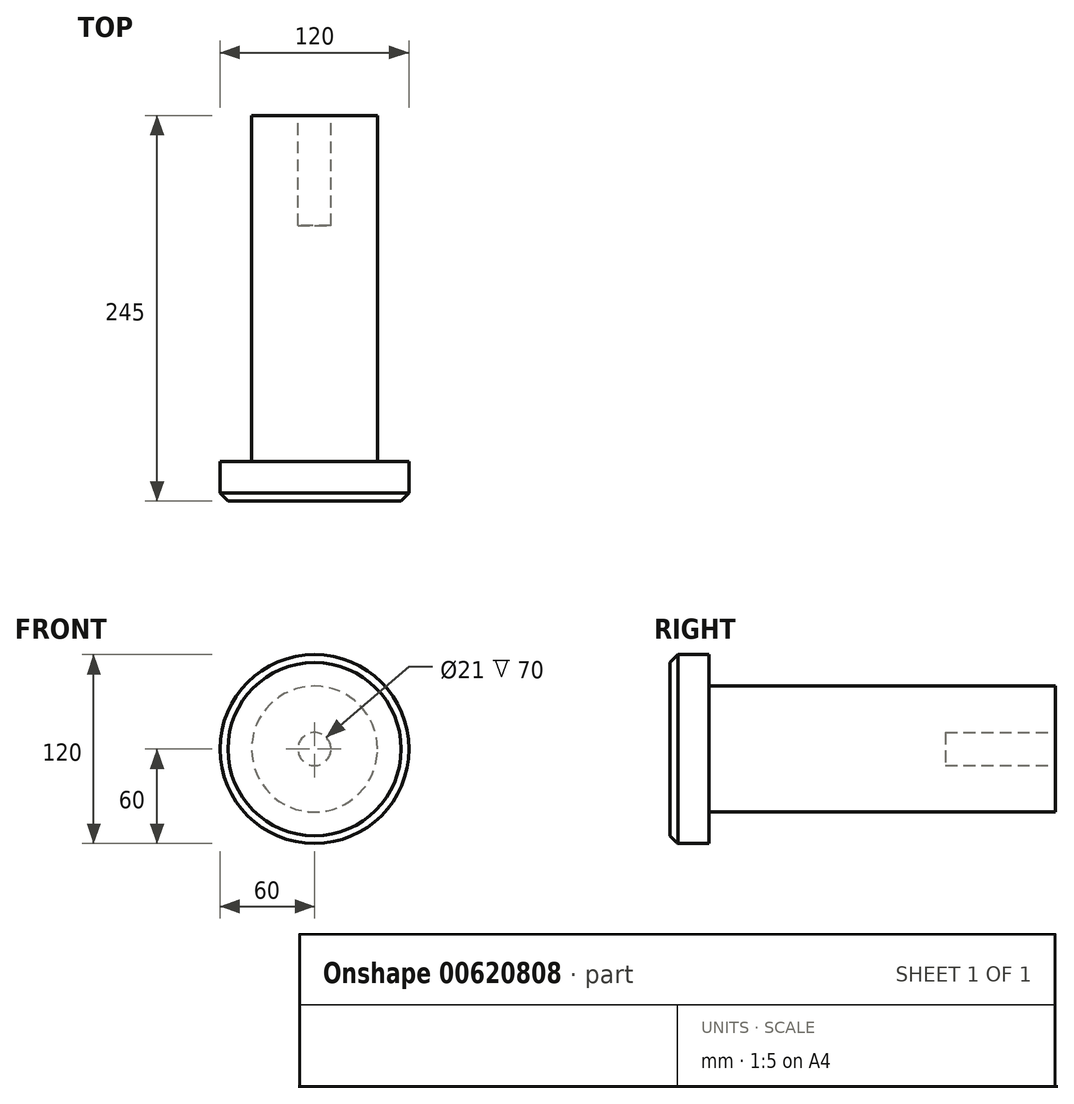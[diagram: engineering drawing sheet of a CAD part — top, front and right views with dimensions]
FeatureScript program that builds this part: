
annotation { "Feature Type Name" : "Feature", "Feature Type Description" : "" }
export const myFeature = defineFeature(function(context is Context, id is Id, definition is map)
    precondition{}
    {
        {
            var Q0;
            Q0=qCreatedBy(makeId("Front.planeOp"),FACE);
            var sketch = newSketch(context, id + "F0", { "sketchPlane" : qUnion([Q0])});
            skCircle(sketch, "E0", {"center": v(0, 0) * mm, "radius": 40 * mm});
            skSolve(sketch);
        }
        {
            var Q0;
            Q0 = qSketchRegion(id + "F0", true);
            extrude(context, id + "F1", {"entities" : qUnion([Q0]), "endBound" : BoundingType.SYMMETRIC, "depth" : 220 * mm, "offsetDistance" : 25 * mm});
        }
        {
            var Q0;
            Q0=makeQuery(id+"F1.opExtrude","CAP_FACE",FACE,{"disambiguationData":[OSD([sQuery(id+"F0.wireOp",EDGE,"E0")])],"isStart":false});
            var sketch = newSketch(context, id + "F2", { "sketchPlane" : qUnion([Q0])});
            skCircle(sketch, "E1", {"center": v(0, 0) * mm, "radius": 60 * mm});
            skSolve(sketch);
        }
        {
            var Q0;
            Q0 = qSketchRegion(id + "F2", true);
            extrude(context, id + "F3", {"entities" : qUnion([Q0]), "operationType" : NewBodyOperationType.ADD, "depth" : 25 * mm, "offsetDistance" : 25 * mm});
        }
        {
            var Q0;
            Q0=makeQuery(id+"F3.opExtrude","CAP_EDGE",EDGE,{"disambiguationData":[OSD([sQuery(id+"F2.wireOp",EDGE,"E1")])],"isStart":false});
            chamfer(context, id + "F4", {"entities" : qUnion([Q0]), "width" : 5 * mm, "tangentPropagation" : true});
        }
        {
            var Q0;
            Q0=makeQuery(id+"F1.opExtrude","CAP_FACE",FACE,{"disambiguationData":[OSD([sQuery(id+"F0.wireOp",EDGE,"E0")])],"isStart":true});
            var sketch = newSketch(context, id + "F5", { "sketchPlane" : qUnion([Q0])});
            skCircle(sketch, "E2", {"center": v(0, 0) * mm, "radius": 10.5 * mm});
            skSolve(sketch);
        }
        {
            var Q0;
            Q0 = qSketchRegion(id + "F5", true);
            extrude(context, id + "F6", {"entities" : qUnion([Q0]), "operationType" : NewBodyOperationType.REMOVE, "oppositeDirection" : true, "depth" : 70 * mm, "offsetDistance" : 25 * mm});
        }
    });
